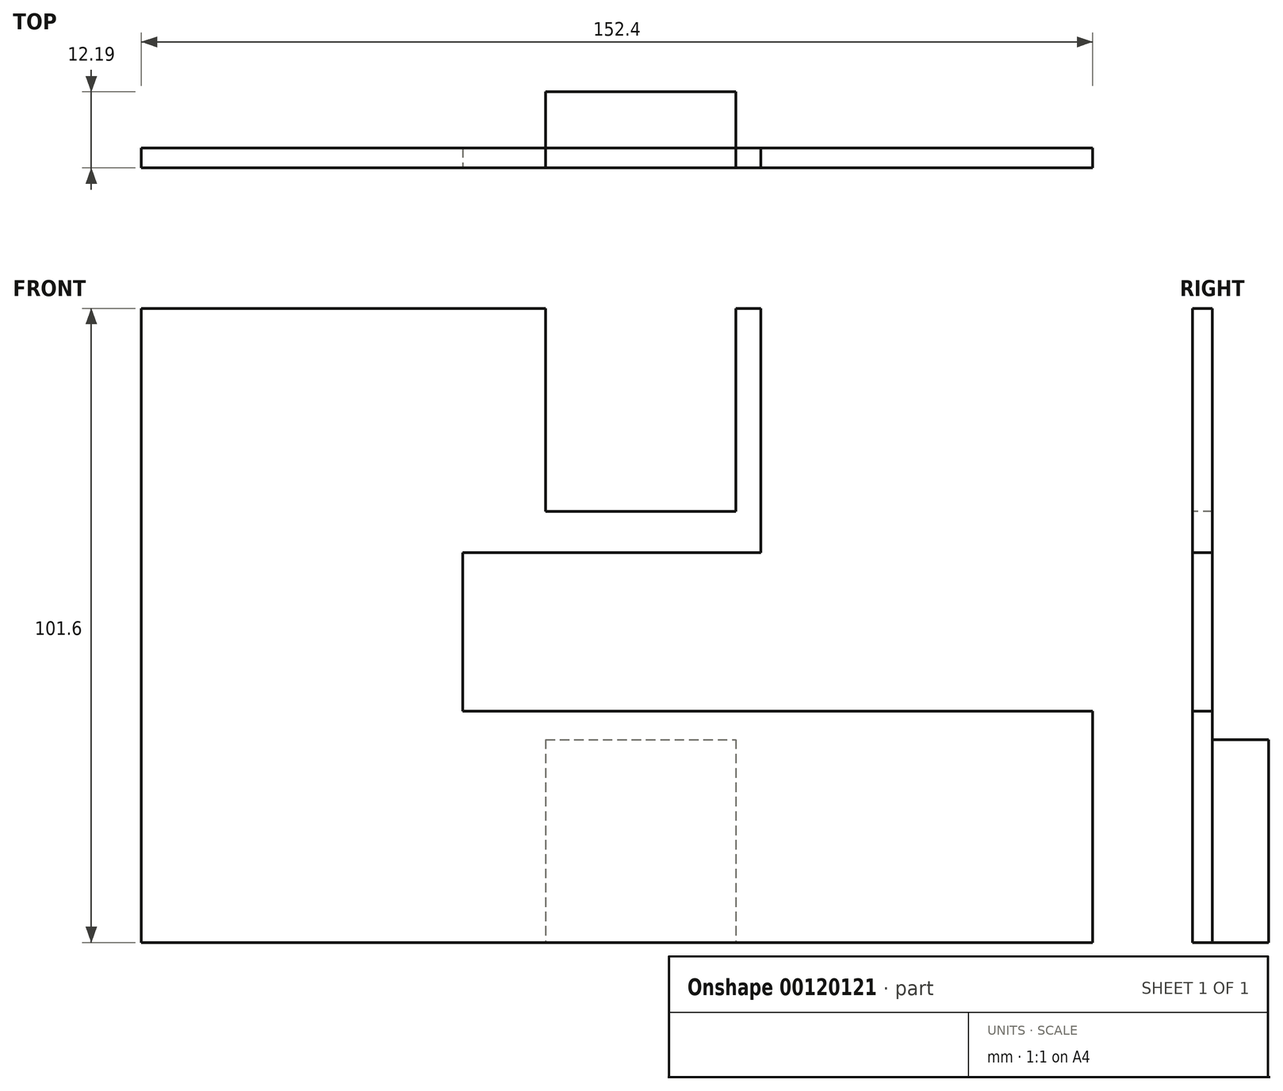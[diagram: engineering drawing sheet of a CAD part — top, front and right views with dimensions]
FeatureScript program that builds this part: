
annotation { "Feature Type Name" : "Feature", "Feature Type Description" : "" }
export const myFeature = defineFeature(function(context is Context, id is Id, definition is map)
    precondition{}
    {
        {
            var Q0;
            Q0=qCreatedBy(makeId("Front.planeOp"),FACE);
            var sketch = newSketch(context, id + "F0", { "sketchPlane" : qUnion([Q0])});
            skLineSegment(sketch, "E0.bottom", {"start": v(-76.44, 48.97) * mm, "end": v(75.96, 48.97) * mm});
            skLineSegment(sketch, "E0.top", {"start": v(-76.44, -52.63) * mm, "end": v(75.96, -52.63) * mm});
            skLineSegment(sketch, "E0.left", {"start": v(-76.44, 48.97) * mm, "end": v(-76.44, -52.63) * mm});
            skLineSegment(sketch, "E0.right", {"start": v(75.96, 48.97) * mm, "end": v(75.96, -52.63) * mm});
            skLineSegment(sketch, "E1.bottom", {"start": v(-11.7, 48.97) * mm, "end": v(18.79, 48.97) * mm});
            skLineSegment(sketch, "E1.top", {"start": v(-11.7, 16.46) * mm, "end": v(18.79, 16.46) * mm});
            skLineSegment(sketch, "E1.left", {"start": v(-11.7, 48.97) * mm, "end": v(-11.7, 16.46) * mm});
            skLineSegment(sketch, "E1.right", {"start": v(18.79, 48.97) * mm, "end": v(18.79, 16.46) * mm});
            skPoint(sketch, "E2", {"position": v(18.79, -20.11) * mm});
            skPoint(sketch, "E3", {"position": v(-11.7, -20.11) * mm});
            skLineSegment(sketch, "E4", {"start": v(-11.7, -20.11) * mm, "end": v(18.79, -20.11) * mm});
            skLineSegment(sketch, "E5", {"start": v(18.79, -20.11) * mm, "end": v(18.79, -52.63) * mm});
            skLineSegment(sketch, "E6", {"start": v(-11.7, -20.11) * mm, "end": v(-11.7, -52.63) * mm});
            skLineSegment(sketch, "E7.bottom", {"start": v(-24.94, -15.55) * mm, "end": v(22.81, -15.55) * mm});
            skLineSegment(sketch, "E7.top", {"start": v(-24.94, 9.85) * mm, "end": v(22.81, 9.85) * mm});
            skLineSegment(sketch, "E7.left", {"start": v(-24.94, -15.55) * mm, "end": v(-24.94, 9.85) * mm});
            skLineSegment(sketch, "E7.right", {"start": v(22.81, -15.55) * mm, "end": v(22.81, 9.85) * mm});
            skLineSegment(sketch, "E8", {"start": v(22.81, -15.55) * mm, "end": v(75.96, -15.55) * mm});
            skLineSegment(sketch, "E9.top", {"start": v(22.81, 60.65) * mm, "end": v(75.96, 60.65) * mm});
            skLineSegment(sketch, "E9.left", {"start": v(22.81, -15.55) * mm, "end": v(22.81, 60.65) * mm});
            skLineSegment(sketch, "E9.right", {"start": v(75.96, -15.55) * mm, "end": v(75.96, 60.65) * mm});
            skSolve(sketch);
        }
        {
            var Q0;
            Q0=makeQuery(id+"F0.imprint","IMPRINT",FACE,{"disambiguationData":[TD([[makeQuery(id+"F0.imprint","IMPRINT",EDGE,{"derivedFrom":sQuery(id+"F0.wireOp",EDGE,"E0.bottom")}),-1.0]])]});
            extrude(context, id + "F1", {"entities" : qUnion([Q0]), "oppositeDirection" : true, "depth" : 3.17 * mm});
        }
        {
            var Q0;
            Q0=makeQuery(id+"F0.imprint","IMPRINT",FACE,{"disambiguationData":[TD([[makeQuery(id+"F0.imprint","IMPRINT",EDGE,{"derivedFrom":sQuery(id+"F0.wireOp",EDGE,"E1.bottom")}),-1.0]])]});
            var Q1;
            Q1=makeQuery(id+"F0.imprint","IMPRINT",FACE,{"disambiguationData":[TD([[makeQuery(id+"F0.imprint","IMPRINT",EDGE,{"derivedFrom":sQuery(id+"F0.wireOp",EDGE,"E4")}),-1.0]])]});
            extrude(context, id + "F2", {"entities" : qUnion([Q0, Q1]), "operationType" : NewBodyOperationType.ADD, "oppositeDirection" : true, "depth" : 12.2 * mm});
        }
    });
